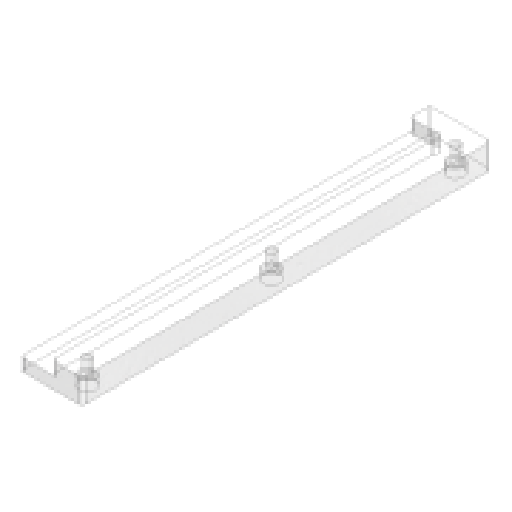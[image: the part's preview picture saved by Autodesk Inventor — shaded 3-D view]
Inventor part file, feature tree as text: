
AUTODESK INVENTOR PART (.ipt)
format: ipt  version: 2025.2 (Build 292293000, 293)  size: 164,864 bytes
history: native  units: in
note: dims shown in document units (in); Inventor stores cm internally (conversion verified against a paired STEP export)
features: sketch x2, extrude x2, hole x1, mirror x1, fillet x1, projected_geometry x1
ambient origin geometry x8: Origin, YZ Plane, XZ Plane, XY Plane, X Axis, Y Axis, Z Axis, Center Point
bodies: Solid1 (feature_tree)
feature tree (8):
  sketch  "Sketch1"  dims[d0=1.1811in d1=7.874in]
  extrude  "Extrusion1"  Depth=7.874in
  extrude  "Extrusion2"  Depth=0.5945in
  hole  "Hole1"  [1 undecoded]
  mirror  "Mirror1"
  fillet  "Fillet1"  Radius=0.2402in
  sketch  "Sketch2"  dims[d2=0.3917in d3=0.5945in d4=0.3937in d5=0.0in d6=0.2402in d7=0.0in d8=7.0866in d9=0.1772in d10=0.2362in d11=0.315in d12=0.1811in d13=90.0deg d14=0.315in d15=0.8108in d16=0.0787in d17=0.2362in d18=0.0787in d22=0.0787in d23=0.5866in d24=0.2953in d25=0.0394in d26=0.3937in]
  projected_geometry  "Projected Loop1"
note: 1 required parameter value undecoded (feature->parameter linkage not recoverable at this tier; creation-order binding heuristic only, values carry confidence <= 0.55)
